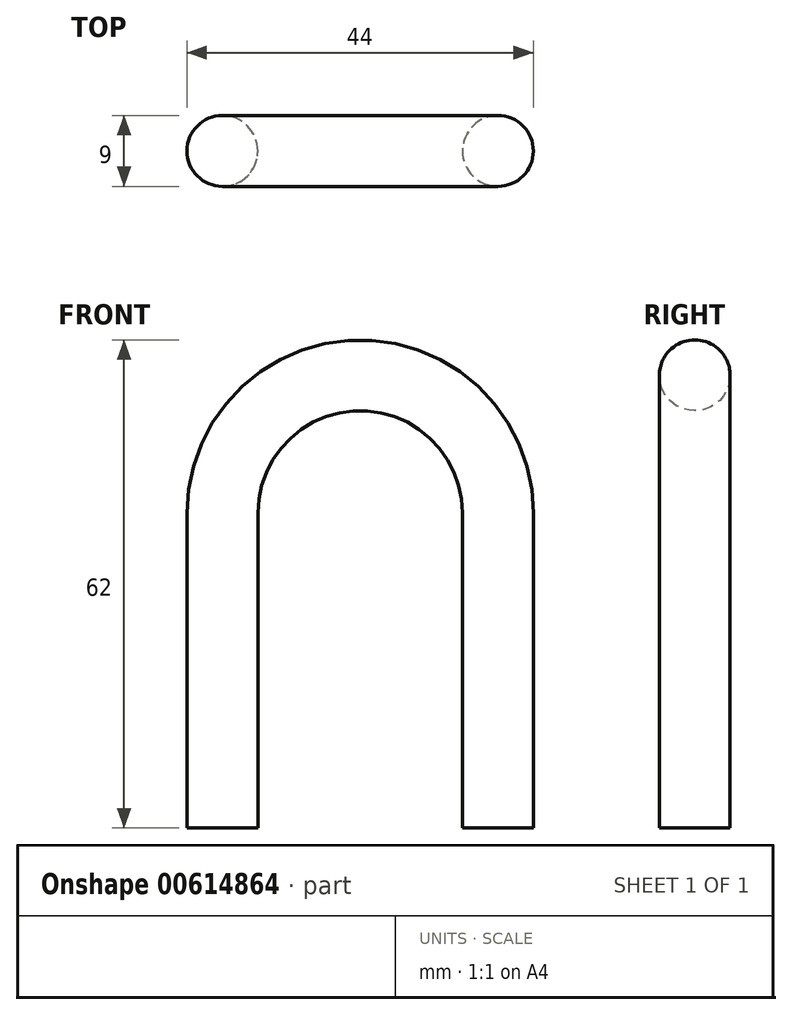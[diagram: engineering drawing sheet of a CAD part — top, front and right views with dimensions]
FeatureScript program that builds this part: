
annotation { "Feature Type Name" : "Feature", "Feature Type Description" : "" }
export const myFeature = defineFeature(function(context is Context, id is Id, definition is map)
    precondition{}
    {
        {
            var Q0;
            Q0=qCreatedBy(makeId("Front.planeOp"),FACE);
            var sketch = newSketch(context, id + "F0", { "sketchPlane" : qUnion([Q0])});
            skLineSegment(sketch, "E0", {"start": v(17.5, 0) * mm, "end": v(17.5, 40) * mm});
            skArc(sketch, "E1", {"start": v(17.5, 40) * mm, "mid": v(0, 57.5) * mm, "end": v(-17.5, 40) * mm});
            skLineSegment(sketch, "E2", {"start": v(-17.5, 40) * mm, "end": v(-17.5, 0) * mm});
            skSolve(sketch);
        }
        {
            var Q0;
            Q0=qCreatedBy(makeId("Top.planeOp"),FACE);
            var sketch = newSketch(context, id + "F1", { "sketchPlane" : qUnion([Q0])});
            skCircle(sketch, "E3", {"center": v(17.5, 0) * mm, "radius": 4.5 * mm});
            skSolve(sketch);
        }
        {
            var Q0;
            Q0=makeQuery(id+"F1.imprint","IMPRINT",FACE,{"disambiguationData":[TD([[makeQuery(id+"F1.imprint","IMPRINT",EDGE,{"derivedFrom":sQuery(id+"F1.wireOp",EDGE,"E3")}),1.0]])]});
            var Q1;
            Q1 = qConstructionFilter(qBodyType(qCreatedBy(id + "F0" ,EDGE), BodyType.WIRE), ConstructionObject.NO);
            sweep(context, id + "F2", {"profiles" : qUnion([Q0]), "path" : qUnion([Q1])});
        }
    });
